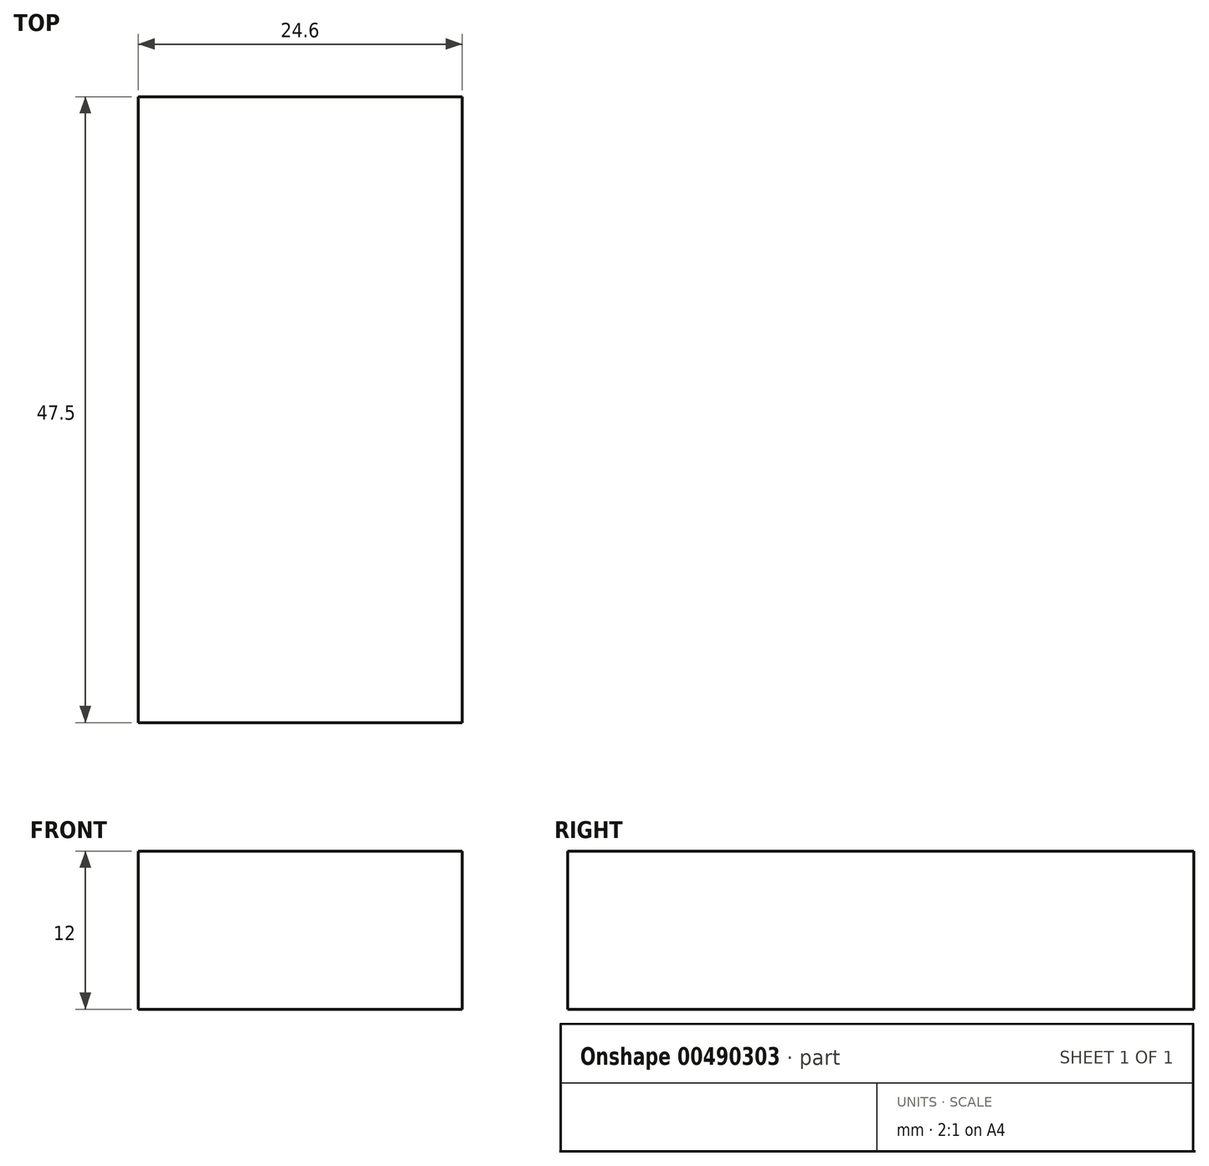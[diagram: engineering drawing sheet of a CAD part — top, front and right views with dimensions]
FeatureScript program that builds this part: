
annotation { "Feature Type Name" : "Feature", "Feature Type Description" : "" }
export const myFeature = defineFeature(function(context is Context, id is Id, definition is map)
    precondition{}
    {
        {
            var Q0;
            Q0=qCreatedBy(makeId("Top.planeOp"),FACE);
            var sketch = newSketch(context, id + "F0", { "sketchPlane" : qUnion([Q0])});
            skLineSegment(sketch, "E0.bottom", {"start": v(12.3, -23.75) * mm, "end": v(-12.3, -23.75) * mm});
            skLineSegment(sketch, "E0.top", {"start": v(12.3, 23.75) * mm, "end": v(-12.3, 23.75) * mm});
            skLineSegment(sketch, "E0.left", {"start": v(12.3, -23.75) * mm, "end": v(12.3, 23.75) * mm});
            skLineSegment(sketch, "E0.right", {"start": v(-12.3, -23.75) * mm, "end": v(-12.3, 23.75) * mm});
            skPoint(sketch, "E0.middle", {"position": v(0, 0) * mm});
            skSolve(sketch);
        }
        {
            var Q0;
            Q0=makeQuery(id+"F0.imprint","IMPRINT",FACE,{"disambiguationData":[TD([[makeQuery(id+"F0.imprint","IMPRINT",EDGE,{"derivedFrom":sQuery(id+"F0.wireOp",EDGE,"E0.bottom")}),-1.0]])]});
            extrude(context, id + "F1", {"entities" : qUnion([Q0]), "depth" : 12 * mm, "offsetDistance" : 25 * mm});
        }
    });
